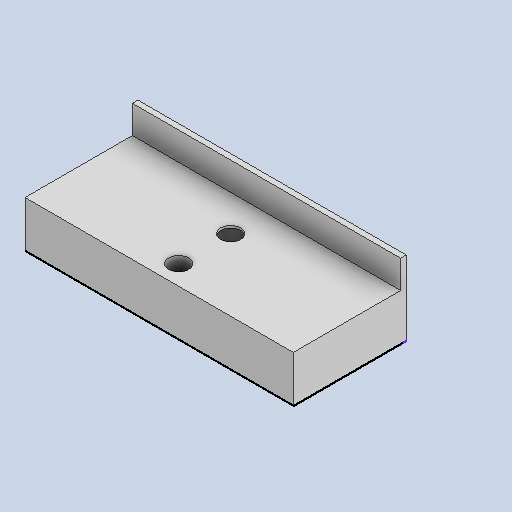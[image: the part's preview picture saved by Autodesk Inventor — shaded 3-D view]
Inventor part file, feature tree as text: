
AUTODESK INVENTOR PART (.ipt)
format: ipt  version: 2024.2 (Build 282272000, 272)  size: 267,264 bytes
history: native  units: in
note: dims shown in document units (in); Inventor stores cm internally (conversion verified against a paired STEP export)
features: extrude x5, sketch x3
ambient origin geometry x8: Origin, YZ Plane, XZ Plane, XY Plane, X Axis, Y Axis, Z Axis, Center Point
bodies: Solid1 (feature_tree)
feature tree (8):
  sketch  "Sketch1"  dims[d0=1.2in d1=2.4in]
  extrude  "Extrusion1"  Depth=2.4in
  extrude  "Extrusion2"  Depth=0.01in
  extrude  "Extrusion3"  Depth=0.175in
  extrude  "Extrusion4"  Depth=0.41in TaperAngle=0.0deg
  extrude  "Extrusion5"  Depth=0.66in TaperAngle=0.0deg
  sketch  "Sketch2"  dims[d2=0.62in d3=0.01in]
  sketch  "Sketch3"  dims[d4=0.29in d5=0.18in d6=0.41in d7=0.0in d8=0.66in d9=0.0in d10=0.29in d11=0.3in d12=0.39in d13=0.0in d14=0.35in d15=0.18in d16=0.41in d17=0.0in d18=0.197in d19=0.197in d20=0.0796in d21=0.0796in d22=0.175in d23=0.0in]
